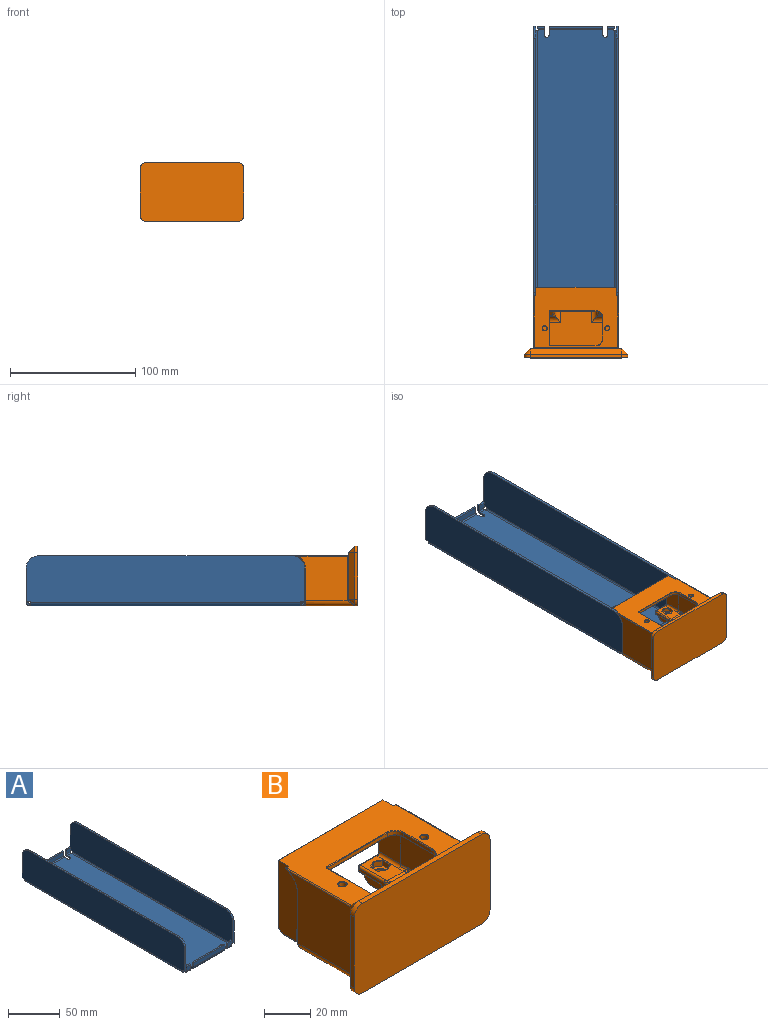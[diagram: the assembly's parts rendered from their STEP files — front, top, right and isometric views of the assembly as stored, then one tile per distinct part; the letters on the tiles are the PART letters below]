
ASSEMBLY  parts=2 mates=1
PART A: 114 faces, bbox 67.7x223x40 mm
  f0: plane 217.4x62.1mm, normal (0,0,-1), area 13406.2mm2, adj f2,f3,f4,f5,f6,f7,f8,f9
  f1: plane 217.4x62.1mm, normal (0,0,1), area 13406.2mm2, adj f2,f3,f4,f5,f6,f7,f8,f9
  f2: cylinder r=2mm len=4mm, axis (0,0,1), area 11.3mm2, adj f0,f1,f3,f13
  f3: plane 4.2x1.8mm, normal (-1,0,0), area 7.6mm2, adj f0,f1,f2,f111
  f4: plane 4.2x1.8mm, normal (1,0,0), area 7.6mm2, adj f0,f1,f5,f110
  f5: cylinder r=2mm len=4mm, axis (0,0,1), area 11.3mm2, adj f0,f1,f4,f6
  f6: plane 4.2x1.8mm, normal (-1,0,0), area 7.6mm2, adj f0,f1,f5,f90
  f7: plane 4.2x1.8mm, normal (-1,0,0), area 7.6mm2, adj f0,f1,f8,f70
  f8: cylinder r=2mm len=4mm, axis (0,0,1), area 11.3mm2, adj f0,f1,f7,f9
  f9: plane 4.2x1.8mm, normal (1,0,0), area 7.6mm2, adj f0,f1,f8,f80
  f10: plane 4.2x1.8mm, normal (-1,0,0), area 7.6mm2, adj f0,f1,f11,f79
  f11: cylinder r=2mm len=4mm, axis (0,0,1), area 11.3mm2, adj f0,f1,f10,f12
  f12: plane 4.2x1.8mm, normal (1,0,0), area 7.6mm2, adj f0,f1,f11,f59
  f13: plane 4.2x1.8mm, normal (1,0,0), area 7.6mm2, adj f0,f1,f2,f101
  f14: plane 1.8x0.71mm, normal (0,1,0), area 1.3mm2, adj f0,f1,f15,f33
  f15: plane 1.8x0.71mm, normal (1,0,0), area 1.3mm2, adj f0,f1,f14,f91
  f16: plane 1.8x0.71mm, normal (1,0,0), area 1.3mm2, adj f0,f1,f17,f71
  f17: plane 1.8x0.71mm, normal (0,-1,0), area 1.3mm2, adj f0,f1,f16,f34
  f18: plane 1.8x0.71mm, normal (0,-1,0), area 1.3mm2, adj f0,f1,f19,f48
  f19: plane 1.8x0.71mm, normal (-1,0,0), area 1.3mm2, adj f0,f1,f18,f60
  f20: plane 1.8x0.71mm, normal (-1,0,0), area 1.3mm2, adj f0,f1,f21,f102
  f21: plane 1.8x0.71mm, normal (0,1,0), area 1.3mm2, adj f0,f1,f20,f49
  f22: plane 26.49x1.8mm, normal (0,1,0), area 47.7mm2, adj f24,f25,f28,f30
  f23: plane 26.49x1.8mm, normal (0,-1,0), area 47.7mm2, adj f24,f25,f27,f32
  f24: plane 223x37.2mm, normal (1,0,0), area 8247.7mm2, adj f22,f23,f26,f27,f28,f29,f30,f31
  f25: plane 223x37.2mm, normal (-1,0,0), area 8247.7mm2, adj f22,f23,f26,f27,f28,f29,f30,f31
  f26: plane 203x1.8mm, normal (0,0,1), area 365.4mm2, adj f24,f25,f27,f28
  f27: cylinder r=10mm len=10mm, axis (1,0,0), area 28.3mm2, adj f23,f24,f25,f26
  f28: cylinder r=10mm len=10mm, axis (-1,0,0), area 28.3mm2, adj f22,f24,f25,f26
  f29: plane 1.8x0.71mm, normal (0,1,0), area 1.3mm2, adj f24,f25,f30,f33
  f30: plane 3.51x1.8mm, normal (0,0,-1), area 6.3mm2, adj f22,f24,f25,f29
  f31: plane 1.8x0.71mm, normal (0,-1,0), area 1.3mm2, adj f24,f25,f32,f34
  f32: plane 3.51x1.8mm, normal (0,0,-1), area 6.3mm2, adj f23,f24,f25,f31
  f33: plane 2.8x2.8mm, normal (0,1,0), area 5.4mm2, adj f14,f29,f35,f36
  f34: plane 2.8x2.8mm, normal (0,-1,0), area 5.4mm2, adj f17,f31,f35,f36
  f35: cylinder r=2.8mm len=215.98mm, axis (0,1,0), area 949.9mm2, adj f0,f24,f33,f34
  f36: cylinder r=1mm len=215.98mm, axis (0,1,0), area 339.3mm2, adj f1,f25,f33,f34
  f37: plane 26.49x1.8mm, normal (0,-1,0), area 47.7mm2, adj f39,f40,f42,f45
  f38: plane 26.49x1.8mm, normal (0,1,0), area 47.7mm2, adj f39,f40,f43,f47
  f39: plane 223x37.2mm, normal (-1,0,0), area 8247.7mm2, adj f37,f38,f41,f42,f43,f44,f45,f46
  f40: plane 223x37.2mm, normal (1,0,0), area 8247.7mm2, adj f37,f38,f41,f42,f43,f44,f45,f46
  f41: plane 203x1.8mm, normal (0,0,1), area 365.4mm2, adj f39,f40,f42,f43
  f42: cylinder r=10mm len=10mm, axis (1,0,0), area 28.3mm2, adj f37,f39,f40,f41
  f43: cylinder r=10mm len=10mm, axis (-1,0,0), area 28.3mm2, adj f38,f39,f40,f41
  f44: plane 1.8x0.71mm, normal (0,-1,0), area 1.3mm2, adj f39,f40,f45,f48
  f45: plane 3.51x1.8mm, normal (0,0,-1), area 6.3mm2, adj f37,f39,f40,f44
  f46: plane 1.8x0.71mm, normal (0,1,0), area 1.3mm2, adj f39,f40,f47,f49
  f47: plane 3.51x1.8mm, normal (0,0,-1), area 6.3mm2, adj f38,f39,f40,f46
  f48: plane 2.8x2.8mm, normal (0,-1,0), area 5.4mm2, adj f18,f44,f50,f51
  f49: plane 2.8x2.8mm, normal (0,1,0), area 5.4mm2, adj f21,f46,f50,f51
  f50: cylinder r=2.8mm len=215.98mm, axis (0,-1,0), area 949.9mm2, adj f0,f39,f48,f49
  f51: cylinder r=1mm len=215.98mm, axis (0,-1,0), area 339.3mm2, adj f1,f40,f48,f49
  f52: plane 4.29x1.8mm, normal (-1,0,0), area 7.7mm2, adj f53,f54,f55,f58
  f53: plane 5.6x5mm, normal (0,-1,0), area 27.5mm2, adj f52,f55,f56,f57,f58,f61
  f54: plane 5.6x5mm, normal (0,1,0), area 27.5mm2, adj f52,f55,f56,f57,f58,f62
  f55: plane 5.6x1.8mm, normal (0,0,1), area 10.1mm2, adj f52,f53,f54,f56
  f56: plane 5x1.8mm, normal (1,0,0), area 9mm2, adj f53,f54,f55,f59
  f57: plane 1.8x0.71mm, normal (-1,0,0), area 1.3mm2, adj f53,f54,f58,f60
  f58: plane 1.8x0.71mm, normal (0,0,-1), area 1.3mm2, adj f52,f53,f54,f57
  f59: plane 2.8x2.8mm, normal (1,0,0), area 5.4mm2, adj f12,f56,f61,f62
  f60: plane 2.8x2.8mm, normal (-1,0,0), area 5.4mm2, adj f19,f57,f61,f62
  f61: cylinder r=2.8mm len=4.89mm, axis (-1,0,0), area 21.5mm2, adj f0,f53,f59,f60
  f62: cylinder r=1mm len=4.89mm, axis (-1,0,0), area 7.7mm2, adj f1,f54,f59,f60
  f63: plane 4.29x1.8mm, normal (1,0,0), area 7.7mm2, adj f64,f65,f66,f69
  f64: plane 5.6x5mm, normal (0,-1,0), area 27.5mm2, adj f63,f66,f67,f68,f69,f72
  f65: plane 5.6x5mm, normal (0,1,0), area 27.5mm2, adj f63,f66,f67,f68,f69,f73
  f66: plane 5.6x1.8mm, normal (0,0,1), area 10.1mm2, adj f63,f64,f65,f67
  f67: plane 5x1.8mm, normal (-1,0,0), area 9mm2, adj f64,f65,f66,f70
  f68: plane 1.8x0.71mm, normal (1,0,0), area 1.3mm2, adj f64,f65,f69,f71
  f69: plane 1.8x0.71mm, normal (0,0,-1), area 1.3mm2, adj f63,f64,f65,f68
  f70: plane 2.8x2.8mm, normal (-1,0,0), area 5.4mm2, adj f7,f67,f72,f73
  f71: plane 2.8x2.8mm, normal (1,0,0), area 5.4mm2, adj f16,f68,f72,f73
  f72: cylinder r=2.8mm len=4.89mm, axis (-1,0,0), area 21.5mm2, adj f0,f64,f70,f71
  f73: cylinder r=1mm len=4.89mm, axis (-1,0,0), area 7.7mm2, adj f1,f65,f70,f71
  f74: plane 42.9x1.8mm, normal (0,0,1), area 77.2mm2, adj f75,f76,f77,f78
  f75: plane 5x1.8mm, normal (-1,0,0), area 9mm2, adj f74,f77,f78,f79
  f76: plane 5x1.8mm, normal (1,0,0), area 9mm2, adj f74,f77,f78,f80
  f77: plane 42.9x5mm, normal (0,-1,0), area 214.5mm2, adj f74,f75,f76,f81
  f78: plane 42.9x5mm, normal (0,1,0), area 214.5mm2, adj f74,f75,f76,f82
  f79: plane 2.8x2.8mm, normal (-1,0,0), area 5.4mm2, adj f10,f75,f81,f82
  f80: plane 2.8x2.8mm, normal (1,0,0), area 5.4mm2, adj f9,f76,f81,f82
  f81: cylinder r=2.8mm len=42.9mm, axis (-1,0,0), area 188.7mm2, adj f0,f77,f79,f80
  f82: cylinder r=1mm len=42.9mm, axis (-1,0,0), area 67.4mm2, adj f1,f78,f79,f80
  f83: plane 4.29x1.8mm, normal (1,0,0), area 7.7mm2, adj f84,f85,f86,f89
  f84: plane 5.6x5mm, normal (0,1,0), area 27.5mm2, adj f83,f86,f87,f88,f89,f92
  f85: plane 5.6x5mm, normal (0,-1,0), area 27.5mm2, adj f83,f86,f87,f88,f89,f93
  f86: plane 5.6x1.8mm, normal (0,0,1), area 10.1mm2, adj f83,f84,f85,f87
  f87: plane 5x1.8mm, normal (-1,0,0), area 9mm2, adj f84,f85,f86,f90
  f88: plane 1.8x0.71mm, normal (1,0,0), area 1.3mm2, adj f84,f85,f89,f91
  f89: plane 1.8x0.71mm, normal (0,0,-1), area 1.3mm2, adj f83,f84,f85,f88
  f90: plane 2.8x2.8mm, normal (-1,0,0), area 5.4mm2, adj f6,f87,f92,f93
  f91: plane 2.8x2.8mm, normal (1,0,0), area 5.4mm2, adj f15,f88,f92,f93
  f92: cylinder r=2.8mm len=4.89mm, axis (1,0,0), area 21.5mm2, adj f0,f84,f90,f91
  f93: cylinder r=1mm len=4.89mm, axis (1,0,0), area 7.7mm2, adj f1,f85,f90,f91
  f94: plane 4.29x1.8mm, normal (-1,0,0), area 7.7mm2, adj f95,f96,f97,f100
  f95: plane 5.6x5mm, normal (0,1,0), area 27.5mm2, adj f94,f97,f98,f99,f100,f103
  f96: plane 5.6x5mm, normal (0,-1,0), area 27.5mm2, adj f94,f97,f98,f99,f100,f104
  f97: plane 5.6x1.8mm, normal (0,0,1), area 10.1mm2, adj f94,f95,f96,f98
  f98: plane 5x1.8mm, normal (1,0,0), area 9mm2, adj f95,f96,f97,f101
  f99: plane 1.8x0.71mm, normal (-1,0,0), area 1.3mm2, adj f95,f96,f100,f102
  f100: plane 1.8x0.71mm, normal (0,0,-1), area 1.3mm2, adj f94,f95,f96,f99
  f101: plane 2.8x2.8mm, normal (1,0,0), area 5.4mm2, adj f13,f98,f103,f104
  f102: plane 2.8x2.8mm, normal (-1,0,0), area 5.4mm2, adj f20,f99,f103,f104
  f103: cylinder r=2.8mm len=4.89mm, axis (1,0,0), area 21.5mm2, adj f0,f95,f101,f102
  f104: cylinder r=1mm len=4.89mm, axis (1,0,0), area 7.7mm2, adj f1,f96,f101,f102
  f105: plane 42.9x1.8mm, normal (0,0,1), area 77.2mm2, adj f106,f107,f108,f109
  f106: plane 5x1.8mm, normal (1,0,0), area 9mm2, adj f105,f108,f109,f110
  f107: plane 5x1.8mm, normal (-1,0,0), area 9mm2, adj f105,f108,f109,f111
  f108: plane 42.9x5mm, normal (0,1,0), area 214.5mm2, adj f105,f106,f107,f112
  f109: plane 42.9x5mm, normal (0,-1,0), area 214.5mm2, adj f105,f106,f107,f113
  f110: plane 2.8x2.8mm, normal (1,0,0), area 5.4mm2, adj f4,f106,f112,f113
  f111: plane 2.8x2.8mm, normal (-1,0,0), area 5.4mm2, adj f3,f107,f112,f113
  f112: cylinder r=2.8mm len=42.9mm, axis (1,0,0), area 188.7mm2, adj f0,f108,f110,f111
  f113: cylinder r=1mm len=42.9mm, axis (1,0,0), area 67.4mm2, adj f1,f109,f110,f111
PART B: 242 faces, bbox 86.8x60.7x51.7 mm
  f0: plane 40.11x35.5mm, normal (-1,0,0), area 1205.6mm2, adj f220,f223,f227,f229,f234,f236
  f1: plane 67x47.5mm, normal (0,0,1), area 1952.4mm2, adj f20,f24,f32,f34,f65,f180,f181,f182
  f2: plane 10.3x7.1mm, normal (0,0,-1), area 56.5mm2, adj f55,f56,f62,f125,f190
  f3: plane 63x33.5mm, normal (0,1,0), area 314.1mm2, adj f6,f55,f64,f65,f66,f74,f75,f76
  f4: plane 10.3x5.7mm, normal (0,-1,0), area 58.7mm2, adj f5,f7,f70,f133
  f5: cylinder r=0.3mm len=10.3mm, axis (-1,0,0), area 4.9mm2, adj f4,f48,f71,f135
  f6: cylinder r=4mm len=10.3mm, axis (-1,0,0), area 64.7mm2, adj f3,f54,f67,f138
  f7: cylinder r=1mm len=10.3mm, axis (1,0,0), area 16.2mm2, adj f4,f54,f69,f134
  f8: cylinder r=1.5mm len=13.23mm, axis (0,-1,0), area 31.1mm2, adj f11,f14,f110,f111
  f9: bspline ~1.74x1.74mm, area 1.9mm2, adj f15,f18,f77,f78,f115,f116
  f10: bspline ~1.06x1.05mm, area 0.3mm2, adj f74,f75,f110
  f11: plane 16.71x10.35mm, normal (0,0,1), area 114.4mm2, adj f8,f74,f104,f105,f106,f107,f108,f109
  f12: cylinder r=2mm len=6.9mm, axis (0,0,-1), area 86.7mm2, adj f97,f190
  f13: cylinder r=2mm len=6.9mm, axis (0,0,-1), area 86.7mm2, adj f188,f189
  f14: plane 23.53x13.53mm, normal (-1,0,0), area 317.2mm2, adj f8,f19,f28,f75,f110
  f15: plane 16.71x10.34mm, normal (0,0,1), area 114.4mm2, adj f9,f78,f98,f99,f100,f101,f102,f103
  f16: plane 10x3.89mm, normal (0,-0.71,0.71), area 53.6mm2, adj f112,f162,f163,f164,f167,f168
  f17: plane 67.21x29.71mm, normal (0,1,0), area 364.5mm2, adj f20,f24,f31,f33,f52,f53,f57,f73
  f18: plane 23.53x13.53mm, normal (1,0,0), area 317.2mm2, adj f9,f19,f27,f77,f116
  f19: plane 63x53.5mm, normal (0,0,-1), area 2065.4mm2, adj f14,f18,f22,f26,f27,f28,f29,f76
  f20: plane 37.5x13.5mm, normal (-1,0,0), area 465.8mm2, adj f1,f17,f33,f34,f57,f58,f59,f60
  f21: plane 73.12x42.12mm, normal (0,0,-1), area 2553mm2, adj f30,f207,f210,f211,f219,f220,f221,f232
  f22: plane 35x20mm, normal (-1,0,0), area 695.1mm2, adj f19,f23,f28,f29,f114
  f23: plane 63x39mm, normal (0,0,1), area 1905.6mm2, adj f22,f26,f29,f79,f80,f81,f82,f114
  f24: plane 37.5x13.5mm, normal (1,0,0), area 465.8mm2, adj f1,f17,f31,f32,f66,f67,f68,f69
  f25: plane 40.11x35.5mm, normal (1,0,0), area 1205.6mm2, adj f221,f222,f226,f228,f237,f239
  f26: plane 35x20mm, normal (1,0,0), area 695.1mm2, adj f19,f23,f27,f29,f120
  f27: plane 33.5x20mm, normal (1,-0.1,0), area 584mm2, adj f18,f19,f26,f117,f118,f119,f120
  f28: plane 33.5x20mm, normal (-1,-0.1,0), area 584mm2, adj f14,f19,f22,f111,f112,f113,f114
  f29: plane 63x35mm, normal (0,1,0), area 2205mm2, adj f19,f22,f23,f26
  f30: plane 83x47.5mm, normal (0,-1,0), area 3921mm2, adj f21,f204,f205,f206,f207,f208,f209,f210
  f31: cylinder r=10mm len=9.61mm, axis (-1,0,0), area 19.3mm2, adj f17,f24,f32,f226
  f32: cylinder r=0.2mm len=1.5mm, axis (-1,0,0), area 0.9mm2, adj f1,f24,f31,f224
  f33: cylinder r=10mm len=9.61mm, axis (1,0,0), area 19.3mm2, adj f17,f20,f34,f227
  f34: cylinder r=0.2mm len=1.5mm, axis (1,0,0), area 0.9mm2, adj f1,f20,f33,f225
  f35: plane 26.5x1.9mm, normal (1,0,0), area 50.4mm2, adj f41,f42,f180,f192
  f36: plane 36.5x1.9mm, normal (0,1,0), area 69.3mm2, adj f42,f44,f183,f196
  f37: plane 17.5x1.9mm, normal (-1,0,0), area 33.3mm2, adj f43,f44,f187,f197
  f38: plane 36.5x1.9mm, normal (0,-1,0), area 69.4mm2, adj f41,f43,f184,f193
  f39: cylinder r=1.75mm len=3.5mm, axis (0,0,1), area 20.9mm2, adj f200,f202
  f40: cylinder r=1.75mm len=3.5mm, axis (0,0,1), area 20.9mm2, adj f199,f201
  f41: cylinder r=0.5mm len=1.9mm, axis (0,0,-1), area 1.5mm2, adj f35,f38,f182,f191
  f42: cylinder r=0.5mm len=1.9mm, axis (0,0,1), area 1.5mm2, adj f35,f36,f181,f194
  f43: cylinder r=5mm len=5mm, axis (0,0,1), area 14.9mm2, adj f37,f38,f186,f195
  f44: cylinder r=5mm len=5mm, axis (0,0,-1), area 14.9mm2, adj f36,f37,f185,f198
  f45: plane 10x3.89mm, normal (0,-0.71,0.71), area 53.6mm2, adj f118,f172,f173,f175,f177,f178
  f46: plane 19.17x4mm, normal (-1,0,0), area 34mm2, adj f82,f153,f154,f155,f157,f159,f164
  f47: plane 19.17x4mm, normal (1,0,0), area 34mm2, adj f79,f143,f145,f147,f148,f149,f175
  f48: plane 13.5x13.5mm, normal (0,0,-1), area 51.8mm2, adj f5,f53,f72,f137,f139,f142,f155
  f49: plane 10.3x5.7mm, normal (0,-1,0), area 58.7mm2, adj f51,f56,f60,f124
  f50: plane 13.75x13.75mm, normal (0,0,-1), area 51.8mm2, adj f51,f52,f58,f128,f130,f132,f147
  f51: cylinder r=0.3mm len=10.3mm, axis (1,0,0), area 4.9mm2, adj f49,f50,f59,f126
  f52: cylinder r=0.3mm len=13.5mm, axis (1,0,0), area 6.4mm2, adj f17,f50,f57,f148
  f53: cylinder r=0.3mm len=13.5mm, axis (1,0,0), area 6.4mm2, adj f17,f48,f73,f154
  f54: plane 10.3x7.1mm, normal (0,0,-1), area 56.5mm2, adj f6,f7,f68,f136,f189
  f55: cylinder r=4mm len=10.3mm, axis (-1,0,0), area 64.7mm2, adj f2,f3,f63,f127
  f56: cylinder r=1mm len=10.3mm, axis (1,0,0), area 16.2mm2, adj f2,f49,f61,f123
  f57: torus R=0.8mm, axis (-1,0,0), area 0.3mm2, adj f17,f20,f52,f58
  f58: cylinder r=0.5mm len=1.3mm, axis (0,-1,0), area 1mm2, adj f20,f50,f57,f59
  f59: torus R=0.8mm, axis (-1,0,0), area 0.6mm2, adj f20,f51,f58,f60
  f60: cylinder r=0.5mm len=5.7mm, axis (0,0,1), area 4.5mm2, adj f20,f49,f59,f61
  f61: torus R=0.5mm, axis (-1,0,0), area 1mm2, adj f20,f56,f60,f62
  f62: cylinder r=0.5mm len=7.1mm, axis (0,1,0), area 5.6mm2, adj f2,f20,f61,f63
  f63: torus R=3.5mm, axis (-1,0,0), area 4.7mm2, adj f20,f55,f62,f64
  f64: cylinder r=0.5mm len=34mm, axis (0,0,1), area 26.5mm2, adj f3,f20,f63,f65
  f65: cylinder r=0.5mm len=64mm, axis (1,0,0), area 49.9mm2, adj f1,f3,f64,f66
  f66: cylinder r=0.5mm len=34mm, axis (0,0,-1), area 26.5mm2, adj f3,f24,f65,f67
  f67: torus R=3.5mm, axis (1,0,0), area 4.7mm2, adj f6,f24,f66,f68
  f68: cylinder r=0.5mm len=7.1mm, axis (0,1,0), area 5.6mm2, adj f24,f54,f67,f69
  f69: torus R=0.5mm, axis (1,0,0), area 1mm2, adj f7,f24,f68,f70
  f70: cylinder r=0.5mm len=5.7mm, axis (0,0,-1), area 4.5mm2, adj f4,f24,f69,f71
  f71: torus R=0.8mm, axis (1,0,0), area 0.6mm2, adj f5,f24,f70,f72
  f72: cylinder r=0.5mm len=1.3mm, axis (0,1,0), area 1mm2, adj f24,f48,f71,f73
  f73: torus R=0.8mm, axis (1,0,0), area 0.3mm2, adj f17,f24,f53,f72
  f74: cylinder r=0.5mm len=12mm, axis (1,0,0), area 8.5mm2, adj f3,f10,f11,f110,f158
  f75: cylinder r=0.5mm len=26mm, axis (0,0,-1), area 19.3mm2, adj f3,f10,f14,f76,f110
  f76: cylinder r=0.5mm len=60mm, axis (1,0,0), area 46.7mm2, adj f3,f19,f75,f77
  f77: cylinder r=0.5mm len=26mm, axis (0,0,1), area 19.3mm2, adj f3,f9,f18,f76,f115
  f78: cylinder r=0.5mm len=12mm, axis (1,0,0), area 8.5mm2, adj f3,f9,f15,f115,f144
  f79: cylinder r=5mm len=13mm, axis (0,-1,0), area 74.9mm2, adj f23,f47,f80,f150,f173
  f80: cylinder r=5mm len=17.39mm, axis (-1,0,0), area 101.9mm2, adj f23,f79,f119,f171,f172,f173
  f81: cylinder r=5mm len=17.39mm, axis (-1,0,0), area 101.9mm2, adj f23,f82,f113,f161,f162,f163
  f82: cylinder r=5mm len=13mm, axis (0,1,0), area 74.9mm2, adj f23,f46,f81,f152,f163
  f83: plane 4.16x2.7mm, normal (1,0,0), area 11.2mm2, adj f84,f88,f89,f107
  f84: plane 3.6x2.7mm, normal (0.5,0.87,0), area 11.2mm2, adj f83,f85,f89,f105
  f85: plane 3.6x2.7mm, normal (-0.5,0.87,0), area 11.2mm2, adj f84,f86,f89,f104
  f86: plane 4.16x2.7mm, normal (-1,0,0), area 11.2mm2, adj f85,f87,f89,f106
  f87: plane 3.6x2.7mm, normal (-0.5,-0.87,0), area 11.2mm2, adj f86,f88,f89,f108
  f88: plane 3.6x2.7mm, normal (0.5,-0.87,0), area 11.2mm2, adj f83,f87,f89,f109
  f89: plane 8.31x7.2mm, normal (0,0,1), area 28.3mm2, adj f83,f84,f85,f86,f87,f88,f188
  f90: plane 8.31x7.2mm, normal (0,0,1), area 28.3mm2, adj f91,f92,f93,f94,f95,f96,f97
  f91: plane 3.6x2.7mm, normal (-0.5,0.87,0), area 11.2mm2, adj f90,f92,f96,f100
  f92: plane 4.16x2.7mm, normal (-1,0,0), area 11.2mm2, adj f90,f91,f93,f98
  f93: plane 3.6x2.7mm, normal (-0.5,-0.87,0), area 11.2mm2, adj f90,f92,f94,f99
  f94: plane 3.6x2.7mm, normal (0.5,-0.87,0), area 11.2mm2, adj f90,f93,f95,f101
  f95: plane 4.16x2.7mm, normal (1,0,0), area 11.2mm2, adj f90,f94,f96,f103
  f96: plane 3.6x2.7mm, normal (0.5,0.87,0), area 11.2mm2, adj f90,f91,f95,f102
  f97: torus R=2.3mm, axis (0,0,1), area 6.2mm2, adj f12,f90
  f98: cylinder r=0.3mm len=4.5mm, axis (0,-1,0), area 2mm2, adj f15,f92,f99,f100
  f99: cylinder r=0.3mm len=4.05mm, axis (0.87,-0.5,0), area 2mm2, adj f15,f93,f98,f101
  f100: cylinder r=0.3mm len=4.05mm, axis (-0.87,-0.5,0), area 2mm2, adj f15,f91,f98,f102
  f101: cylinder r=0.3mm len=4.05mm, axis (0.87,0.5,0), area 2mm2, adj f15,f94,f99,f103
  f102: cylinder r=0.3mm len=4.05mm, axis (-0.87,0.5,0), area 2mm2, adj f15,f96,f100,f103
  f103: cylinder r=0.3mm len=4.5mm, axis (0,1,0), area 2mm2, adj f15,f95,f101,f102
  f104: cylinder r=0.3mm len=4.05mm, axis (-0.87,-0.5,0), area 2mm2, adj f11,f85,f105,f106
  f105: cylinder r=0.3mm len=4.05mm, axis (-0.87,0.5,0), area 2mm2, adj f11,f84,f104,f107
  f106: cylinder r=0.3mm len=4.5mm, axis (0,-1,0), area 2mm2, adj f11,f86,f104,f108
  f107: cylinder r=0.3mm len=4.5mm, axis (0,1,0), area 2mm2, adj f11,f83,f105,f109
  f108: cylinder r=0.3mm len=4.05mm, axis (0.87,-0.5,0), area 2mm2, adj f11,f87,f106,f109
  f109: cylinder r=0.3mm len=4.05mm, axis (0.87,0.5,0), area 2mm2, adj f11,f88,f107,f108
  f110: bspline ~1.74x1.74mm, area 1.9mm2, adj f8,f10,f11,f14,f74,f75
  f111: cylinder r=1.5mm len=4.7mm, axis (0.1,-1,0), area 8.5mm2, adj f8,f11,f28,f168,f169
  f112: cylinder r=1.5mm len=6.99mm, axis (0.07,-0.71,-0.71), area 14.8mm2, adj f16,f28,f160,f161,f169
  f113: bspline ~5.82x5mm, area 15.9mm2, adj f28,f81,f114,f160
  f114: cylinder r=1.5mm len=21.22mm, axis (0.1,-1,0), area 27.4mm2, adj f22,f23,f28,f113
  f115: bspline ~1.17x1.17mm, area 0.3mm2, adj f9,f77,f78
  f116: cylinder r=1.5mm len=13.23mm, axis (0,1,0), area 31.1mm2, adj f9,f15,f18,f117
  f117: cylinder r=1.5mm len=4.7mm, axis (0.1,1,0), area 8.5mm2, adj f15,f27,f116,f178,f179
  f118: cylinder r=1.5mm len=6.99mm, axis (-0.07,-0.71,-0.71), area 14.8mm2, adj f27,f45,f170,f171,f179
  f119: bspline ~6.51x5.87mm, area 15.9mm2, adj f27,f80,f120,f170
  f120: cylinder r=1.5mm len=21.22mm, axis (0.1,1,0), area 27.4mm2, adj f23,f26,f27,f119
  f121: plane 11.71x6.6mm, normal (-1,0,0), area 74mm2, adj f133,f134,f135,f136,f138,f139,f140
  f122: plane 11.71x6.6mm, normal (1,0,0), area 74mm2, adj f123,f124,f125,f126,f127,f129,f130
  f123: torus R=0.8mm, axis (-1,0,0), area 0.5mm2, adj f56,f122,f124,f125
  f124: cylinder r=0.2mm len=5.7mm, axis (0,0,1), area 1.8mm2, adj f49,f122,f123,f126
  f125: cylinder r=0.2mm len=7.1mm, axis (0,1,0), area 2.2mm2, adj f2,f122,f123,f127
  f126: torus R=0.5mm, axis (-1,0,0), area 0.1mm2, adj f51,f122,f124,f128
  f127: torus R=3.8mm, axis (-1,0,0), area 1.9mm2, adj f55,f122,f125,f129
  f128: bspline ~0.57x0.4mm, area 0.1mm2, adj f50,f126,f130
  f129: cylinder r=0.2mm len=2.8mm, axis (0,0,-1), area 0.9mm2, adj f3,f122,f127,f131
  f130: cylinder r=0.2mm len=11.71mm, axis (0,1,0), area 3.7mm2, adj f50,f122,f128,f131
  f131: torus R=0.4mm, axis (0,-1,0), area 0.1mm2, adj f3,f129,f130,f132
  f132: cylinder r=0.2mm len=2.8mm, axis (-1,0,0), area 0.9mm2, adj f3,f50,f131,f146
  f133: cylinder r=0.2mm len=5.7mm, axis (0,0,-1), area 1.8mm2, adj f4,f121,f134,f135
  f134: torus R=0.8mm, axis (-1,0,0), area 0.5mm2, adj f7,f121,f133,f136
  f135: torus R=0.5mm, axis (-1,0,0), area 0.1mm2, adj f5,f121,f133,f137
  f136: cylinder r=0.2mm len=7.1mm, axis (0,-1,0), area 2.2mm2, adj f54,f121,f134,f138
  f137: bspline ~0.57x0.4mm, area 0.1mm2, adj f48,f135,f139
  f138: torus R=3.8mm, axis (-1,0,0), area 1.9mm2, adj f6,f121,f136,f140
  f139: cylinder r=0.2mm len=11.71mm, axis (0,1,0), area 3.7mm2, adj f48,f121,f137,f141
  f140: cylinder r=0.2mm len=2.8mm, axis (0,0,1), area 0.9mm2, adj f3,f121,f138,f141
  f141: torus R=0.4mm, axis (0,-1,0), area 0.1mm2, adj f3,f139,f140,f142
  f142: cylinder r=0.2mm len=2.8mm, axis (1,0,0), area 0.9mm2, adj f3,f48,f141,f156
  f143: cylinder r=1mm len=15.67mm, axis (0,-1,0), area 24.2mm2, adj f15,f47,f144,f174
  f144: bspline ~1.05x1mm, area 0.5mm2, adj f78,f143,f145
  f145: cylinder r=1mm len=2.8mm, axis (0,0,1), area 3.4mm2, adj f3,f47,f144,f146
  f146: bspline ~1.04x1mm, area 0.2mm2, adj f132,f145,f147
  f147: cylinder r=1mm len=13.5mm, axis (0,-1,0), area 20.6mm2, adj f47,f50,f146,f148
  f148: torus R=1.3mm, axis (-1,0,0), area 1.6mm2, adj f47,f52,f147,f149
  f149: cylinder r=1mm len=1.2mm, axis (0,0,1), area 1.9mm2, adj f17,f47,f148,f150
  f150: torus R=6mm, axis (0,-1,0), area 13.2mm2, adj f17,f79,f149,f151
  f151: cylinder r=1mm len=24mm, axis (-1,0,0), area 37.7mm2, adj f17,f23,f150,f152
  f152: torus R=6mm, axis (0,-1,0), area 13.2mm2, adj f17,f82,f151,f153
  f153: cylinder r=1mm len=1.2mm, axis (0,0,-1), area 1.9mm2, adj f17,f46,f152,f154
  f154: torus R=1.3mm, axis (-1,0,0), area 1.6mm2, adj f46,f53,f153,f155
  f155: cylinder r=1mm len=13.5mm, axis (0,-1,0), area 20.6mm2, adj f46,f48,f154,f156
  f156: bspline ~1.04x1mm, area 0.2mm2, adj f142,f155,f157
  f157: cylinder r=1mm len=2.8mm, axis (0,0,-1), area 3.4mm2, adj f3,f46,f156,f158
  f158: bspline ~1.05x1mm, area 0.5mm2, adj f74,f157,f159
  f159: cylinder r=1mm len=15.67mm, axis (0,1,0), area 24.2mm2, adj f11,f46,f158,f165
  f160: bspline ~1.93x1.87mm, area 1.2mm2, adj f112,f113,f161
  f161: bspline ~1.17x0.57mm, area 0.1mm2, adj f81,f112,f160,f162
  f162: cylinder r=2mm len=11.41mm, axis (-1,0,0), area 14.1mm2, adj f16,f81,f161,f163
  f163: bspline ~6.4x5.32mm, area 7.8mm2, adj f16,f81,f82,f162,f164
  f164: cylinder r=2mm len=5.41mm, axis (0,0.71,0.71), area 15.6mm2, adj f16,f46,f163,f165,f166
  f165: bspline ~1.5x1.29mm, area 1.8mm2, adj f11,f159,f164,f166
  f166: bspline ~1.68x1.59mm, area 0.6mm2, adj f164,f165,f167
  f167: cylinder r=2mm len=10.02mm, axis (-1,0,0), area 15.2mm2, adj f11,f16,f166,f168
  f168: bspline ~1.41x0.59mm, area 0.3mm2, adj f16,f111,f167,f169
  f169: bspline ~2.08x1.69mm, area 1.4mm2, adj f111,f112,f168
  f170: bspline ~1.93x1.63mm, area 1.2mm2, adj f118,f119,f171
  f171: bspline ~1.17x0.58mm, area 0.1mm2, adj f80,f118,f170,f172
  f172: cylinder r=2mm len=11.41mm, axis (-1,0,0), area 14.1mm2, adj f45,f80,f171,f173
  f173: bspline ~4.91x3.91mm, area 7.8mm2, adj f45,f79,f80,f172,f175
  f174: bspline ~2.12x1.53mm, area 1.8mm2, adj f15,f143,f175,f176
  f175: cylinder r=2mm len=5.41mm, axis (0,-0.71,-0.71), area 15.6mm2, adj f45,f47,f173,f174,f176
  f176: bspline ~1.68x1.59mm, area 0.6mm2, adj f174,f175,f177
  f177: cylinder r=2mm len=10.02mm, axis (-1,0,0), area 15.2mm2, adj f15,f45,f176,f178
  f178: bspline ~1.41x0.59mm, area 0.3mm2, adj f45,f117,f177,f179
  f179: bspline ~2.08x1.69mm, area 1.4mm2, adj f117,f118,f178
  f180: cylinder r=0.3mm len=26.5mm, axis (0,1,0), area 12.5mm2, adj f1,f35,f181,f182
  f181: torus R=0.8mm, axis (0,0,1), area 0.5mm2, adj f1,f42,f180,f183
  f182: torus R=0.8mm, axis (0,0,1), area 0.5mm2, adj f1,f41,f180,f184
  f183: cylinder r=0.3mm len=36.5mm, axis (-1,0,0), area 17.2mm2, adj f1,f36,f181,f185
  f184: cylinder r=0.3mm len=36.5mm, axis (1,0,0), area 17.2mm2, adj f1,f38,f182,f186
  f185: torus R=5.3mm, axis (0,0,1), area 3.8mm2, adj f1,f44,f183,f187
  f186: torus R=5.3mm, axis (0,0,1), area 3.8mm2, adj f1,f43,f184,f187
  f187: cylinder r=0.3mm len=17.5mm, axis (0,-1,0), area 8.2mm2, adj f1,f37,f185,f186
  f188: torus R=2.3mm, axis (0,0,1), area 6.2mm2, adj f13,f89
  f189: torus R=2.3mm, axis (0,0,1), area 6.2mm2, adj f13,f54
  f190: torus R=2.3mm, axis (0,0,1), area 6.2mm2, adj f2,f12
  f191: torus R=0.8mm, axis (0,0,-1), area 0.5mm2, adj f19,f41,f192,f193
  f192: cylinder r=0.3mm len=26.5mm, axis (0,-1,0), area 12.5mm2, adj f19,f35,f191,f194
  f193: cylinder r=0.3mm len=36.5mm, axis (-1,0,0), area 17.2mm2, adj f19,f38,f191,f195
  f194: torus R=0.8mm, axis (0,0,-1), area 0.5mm2, adj f19,f42,f192,f196
  f195: torus R=5.3mm, axis (0,0,-1), area 3.8mm2, adj f19,f43,f193,f197
  f196: cylinder r=0.3mm len=36.5mm, axis (1,0,0), area 17.2mm2, adj f19,f36,f194,f198
  f197: cylinder r=0.3mm len=17.5mm, axis (0,1,0), area 8.2mm2, adj f19,f37,f195,f198
  f198: torus R=5.3mm, axis (0,0,-1), area 3.8mm2, adj f19,f44,f196,f197
  f199: torus R=2.05mm, axis (0,0,-1), area 5.5mm2, adj f19,f40
  f200: torus R=2.05mm, axis (0,0,-1), area 5.5mm2, adj f19,f39
  f201: torus R=2.05mm, axis (0,0,1), area 5.5mm2, adj f1,f40
  f202: torus R=2.05mm, axis (0,0,1), area 5.5mm2, adj f1,f39
  f203: plane 73x37.5mm, normal (0,1,0), area 218.5mm2, adj f211,f213,f215,f217,f219,f236,f238,f239
  f204: plane 73x2.5mm, normal (0,0,1), area 182.5mm2, adj f30,f208,f209,f215
  f205: plane 37.5x2.5mm, normal (1,0,0), area 93.8mm2, adj f30,f209,f210,f213
  f206: plane 37.5x2.5mm, normal (-1,0,0), area 93.8mm2, adj f30,f207,f208,f217
  f207: cylinder r=5mm len=5mm, axis (0,1,0), area 19.6mm2, adj f21,f30,f206,f218
  f208: cylinder r=5mm len=5mm, axis (0,1,0), area 19.6mm2, adj f30,f204,f206,f216
  f209: cylinder r=5mm len=5mm, axis (0,1,0), area 19.6mm2, adj f30,f204,f205,f214
  f210: cylinder r=5mm len=5mm, axis (0,1,0), area 19.6mm2, adj f21,f30,f205,f212
  f211: plane 5x5mm, normal (0,0.71,-0.71), area 16.6mm2, adj f21,f203,f212,f235,f237
  f212: cone r=5mm half-angle=45deg, axis (0,-1,0), area 18.5mm2, adj f210,f211,f213
  f213: plane 41.33x8.83mm, normal (0.71,0.71,0), area 265.2mm2, adj f203,f205,f212,f214
  f214: cone r=5mm half-angle=45deg, axis (0,-1,0), area 37mm2, adj f209,f213,f215
  f215: plane 73x5mm, normal (0,0.71,0.71), area 516.2mm2, adj f203,f204,f214,f216
  f216: cone r=5mm half-angle=45deg, axis (0,-1,0), area 27.8mm2, adj f208,f215,f217
  f217: plane 37.5x5mm, normal (-0.71,0.71,0), area 265.2mm2, adj f203,f206,f216,f218
  f218: cone r=5mm half-angle=45deg, axis (0,-1,0), area 27.8mm2, adj f207,f217,f219
  f219: plane 5x5mm, normal (0,0.71,-0.71), area 16.6mm2, adj f21,f203,f218,f233,f234
  f220: cylinder r=4mm len=39.09mm, axis (0,1,0), area 229.9mm2, adj f0,f21,f231,f233
  f221: cylinder r=4mm len=39.09mm, axis (0,1,0), area 229.9mm2, adj f21,f25,f230,f235
  f222: cylinder r=0.5mm len=41.17mm, axis (0,1,0), area 31.7mm2, adj f1,f25,f224,f241
  f223: cylinder r=0.5mm len=41.17mm, axis (0,1,0), area 31.7mm2, adj f0,f1,f225,f238
  f224: bspline ~3.06x1.05mm, area 0.4mm2, adj f32,f222,f226
  f225: bspline ~3.06x1.05mm, area 0.4mm2, adj f34,f223,f227
  f226: torus R=10.5mm, axis (1,0,0), area 9.7mm2, adj f25,f31,f224,f228
  f227: torus R=10.5mm, axis (-1,0,0), area 9.7mm2, adj f0,f33,f225,f229
  f228: cylinder r=0.5mm len=26mm, axis (0,0,1), area 20.4mm2, adj f17,f25,f226,f230
  f229: cylinder r=0.5mm len=26mm, axis (0,0,-1), area 20.4mm2, adj f0,f17,f227,f231
  f230: torus R=3.5mm, axis (0,-1,0), area 4.7mm2, adj f17,f221,f228,f232
  f231: torus R=3.5mm, axis (0,-1,0), area 4.7mm2, adj f17,f220,f229,f232
  f232: cylinder r=0.5mm len=60mm, axis (1,0,0), area 47.1mm2, adj f17,f21,f230,f231
  f233: bspline ~5.71x5mm, area 9.3mm2, adj f21,f219,f220,f234
  f234: cylinder r=1mm len=1.29mm, axis (0,0.71,0.71), area 1mm2, adj f0,f219,f233,f236
  f235: bspline ~5.71x5mm, area 9.3mm2, adj f21,f211,f221,f237
  f236: cylinder r=1mm len=34.91mm, axis (0,0,-1), area 54.5mm2, adj f0,f203,f234,f238
  f237: cylinder r=1mm len=1.29mm, axis (0,-0.71,-0.71), area 1mm2, adj f25,f211,f235,f239
  f238: torus R=1.5mm, axis (0,1,0), area 2.1mm2, adj f203,f223,f236,f240
  f239: cylinder r=1mm len=34.91mm, axis (0,0,-1), area 54.5mm2, adj f25,f203,f237,f241
  f240: cylinder r=1mm len=67mm, axis (-1,0,0), area 105.2mm2, adj f1,f203,f238,f241
  f241: torus R=1.5mm, axis (0,1,0), area 2.1mm2, adj f203,f222,f239,f240
PLACE A t=(-23.2,-87.95,35.95)mm
PLACE B t=(-25.59,-52.27,24.72)mm
MATE cylindrical A.f27 <-> B.f31  axis (1,0,0) through (-58.4,-42.27,25.95)mm
